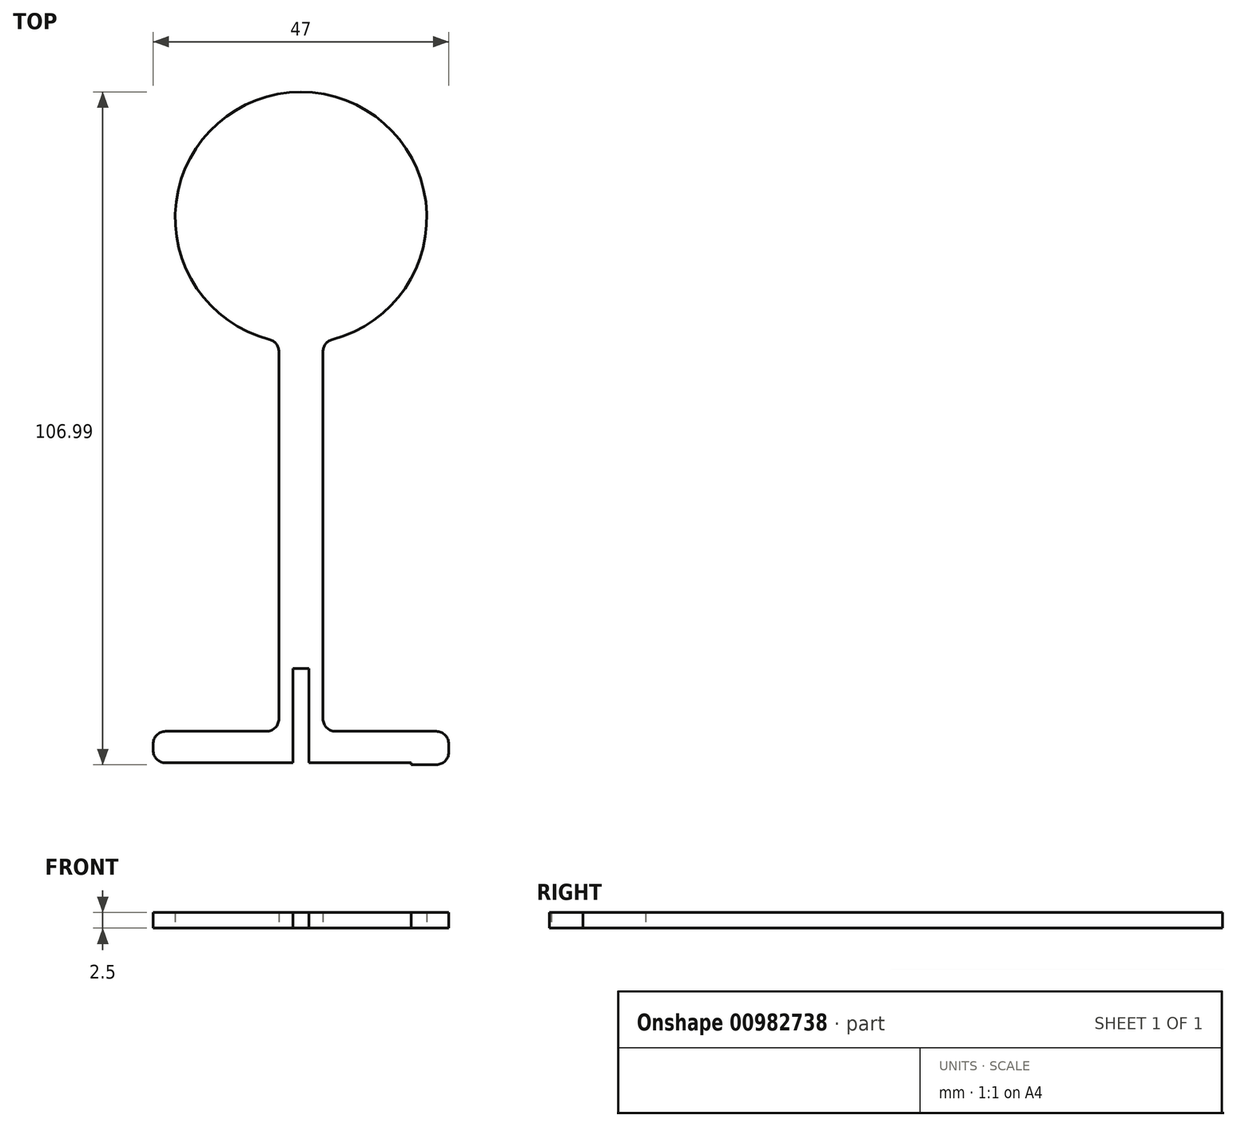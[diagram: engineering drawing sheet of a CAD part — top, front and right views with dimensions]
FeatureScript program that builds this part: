
annotation { "Feature Type Name" : "Feature", "Feature Type Description" : "" }
export const myFeature = defineFeature(function(context is Context, id is Id, definition is map)
    precondition{}
    {
        {
            var Q0;
            Q0=qCreatedBy(makeId("Top.planeOp"),FACE);
            var sketch = newSketch(context, id + "F0", { "sketchPlane" : qUnion([Q0])});
            skLineSegment(sketch, "E0", {"start": v(-3.5, -3) * mm, "end": v(-3.5, -65) * mm});
            skLineSegment(sketch, "E1", {"start": v(-3.5, -65) * mm, "end": v(-23.5, -65) * mm});
            skLineSegment(sketch, "E2", {"start": v(-23.5, -65) * mm, "end": v(-23.5, -70) * mm});
            skLineSegment(sketch, "E3", {"start": v(-23.5, -70) * mm, "end": v(23.5, -70) * mm});
            skLineSegment(sketch, "E4", {"start": v(23.5, -70) * mm, "end": v(23.5, -65) * mm});
            skLineSegment(sketch, "E5", {"start": v(23.5, -65) * mm, "end": v(3.5, -65) * mm});
            skLineSegment(sketch, "E6", {"start": v(3.5, -65) * mm, "end": v(3.5, -3) * mm});
            skLineSegment(sketch, "E7.bottom", {"start": v(1.25, -70) * mm, "end": v(-1.25, -70) * mm});
            skLineSegment(sketch, "E7.top", {"start": v(1.25, -55) * mm, "end": v(-1.25, -55) * mm});
            skLineSegment(sketch, "E7.left", {"start": v(1.25, -70) * mm, "end": v(1.25, -55) * mm});
            skLineSegment(sketch, "E7.right", {"start": v(-1.25, -70) * mm, "end": v(-1.25, -55) * mm});
            skPoint(sketch, "E7.middle", {"position": v(0, -62.5) * mm});
            skCircle(sketch, "E8", {"center": v(0, 16.7) * mm, "radius": 20 * mm});
            skLineSegment(sketch, "E9.bottom", {"start": v(-23.5, -70) * mm, "end": v(-17.5, -70) * mm});
            skLineSegment(sketch, "E9.top", {"start": v(-23.5, -70.3) * mm, "end": v(-17.5, -70.3) * mm});
            skLineSegment(sketch, "E9.left", {"start": v(-23.5, -70) * mm, "end": v(-23.5, -70.3) * mm});
            skLineSegment(sketch, "E9.right", {"start": v(-17.5, -70) * mm, "end": v(-17.5, -70.3) * mm});
            skLineSegment(sketch, "E10.MirrorCS", {"start": v(23.5, -70.3) * mm, "end": v(17.5, -70.3) * mm});
            skLineSegment(sketch, "E11.MirrorCS", {"start": v(23.5, -70) * mm, "end": v(17.5, -70) * mm});
            skLineSegment(sketch, "E12.MirrorCS", {"start": v(23.5, -70) * mm, "end": v(23.5, -70.3) * mm});
            skLineSegment(sketch, "E13.MirrorCS", {"start": v(17.5, -70) * mm, "end": v(17.5, -70.3) * mm});
            skSolve(sketch);
        }
        {
            var Q0;
            Q0=makeQuery(id+"F0.imprint","IMPRINT",FACE,{"disambiguationData":[TD([[makeQuery(id+"F0.imprint","IMPRINT",EDGE,{"derivedFrom":sQuery(id+"F0.wireOp",EDGE,"0U4RxweM-u2bA-2Qqt-OOBg-x1ftkZs6jUrD")}),1.0]])]});
            var Q1;
            {var subQ0=sQuery(id+"F0.wireOp",EDGE,"im0v1Rov-prSM-cwdN-f0IW-ScqFdnQkXUSi");Q1=makeQuery(id+"F0.imprint","IMPRINT",FACE,{"disambiguationData":[TD([[makeQuery(id+"F0.imprint","IMPRINT",EDGE,{"derivedFrom":subQ0}),1.0]])]});}
            var Q2;
            {var subQ7=sQuery(id+"F0.wireOp",EDGE,"E0");Q2=makeQuery(id+"F0.imprint","IMPRINT",FACE,{"disambiguationData":[TD([[makeQuery(id+"F0.imprint","IMPRINT",EDGE,{"derivedFrom":subQ7}),1.0]])]});}
            var Q3;
            {var subQ0=sQuery(id+"F0.wireOp",EDGE,"E8");var subQ1=makeQuery(id+"F0.imprint","INTERSECT",VERTEX,{"derivedFrom":[sQuery(id+"F0.wireOp",EDGE,"E0"),subQ0]});Q3=makeQuery(id+"F0.imprint","IMPRINT",FACE,{"disambiguationData":[TD([[makeQuery(id+"F0.imprint","IMPRINT",EDGE,{"disambiguationData":[TD([[subQ1,-1.0]])],"derivedFrom":subQ0}),1.0]])]});}
            var Q4;
            Q4=makeQuery(id+"F0.imprint","IMPRINT",FACE,{"disambiguationData":[TD([[makeQuery(id+"F0.imprint","IMPRINT",EDGE,{"derivedFrom":sQuery(id+"F0.wireOp",EDGE,"E9.bottom")}),-1.0]])]});
            var Q5;
            Q5=makeQuery(id+"F0.imprint","IMPRINT",FACE,{"disambiguationData":[TD([[makeQuery(id+"F0.imprint","IMPRINT",EDGE,{"derivedFrom":sQuery(id+"F0.wireOp",EDGE,"E10.MirrorCS")}),-1.0]])]});
            extrude(context, id + "F1", {"entities" : qUnion([Q0, Q1, Q2, Q3, Q4, Q5]), "flatOperationType" : FlatOperationType.REMOVE, "depth" : 2.5 * mm, "offsetDistance" : 25 * mm, "domain" : OperationDomain.MODEL});
        }
        {
            var Q0;
            Q0=makeQuery(id+"F1.opExtrude","SWEPT_EDGE",EDGE,{"disambiguationData":[OSD([sQuery(id+"F0.wireOp",EDGE,"E0"),sQuery(id+"F0.wireOp",EDGE,"E8")])]});
            var Q1;
            Q1=makeQuery(id+"F1.opExtrude","SWEPT_EDGE",EDGE,{"disambiguationData":[OSD([sQuery(id+"F0.wireOp",EDGE,"E6"),sQuery(id+"F0.wireOp",EDGE,"E8")])]});
            var Q2;
            Q2=makeQuery(id+"F1.opExtrude","SWEPT_EDGE",EDGE,{"disambiguationData":[OSD([sQuery(id+"F0.wireOp",EDGE,"E4"),sQuery(id+"F0.wireOp",EDGE,"E5")])]});
            var Q3;
            Q3=makeQuery(id+"F1.opExtrude","SWEPT_EDGE",EDGE,{"disambiguationData":[OSD([sQuery(id+"F0.wireOp",EDGE,"E1"),sQuery(id+"F0.wireOp",EDGE,"E2")])]});
            var Q4;
            Q4=makeQuery(id+"F1.opExtrude","SWEPT_EDGE",EDGE,{"disambiguationData":[OSD([sQuery(id+"F0.wireOp",EDGE,"E0"),sQuery(id+"F0.wireOp",EDGE,"E1")])]});
            var Q5;
            Q5=makeQuery(id+"F1.opExtrude","SWEPT_EDGE",EDGE,{"disambiguationData":[OSD([sQuery(id+"F0.wireOp",EDGE,"E5"),sQuery(id+"F0.wireOp",EDGE,"E6")])]});
            var Q6;
            Q6=makeQuery(id+"F1.opExtrude","SWEPT_EDGE",EDGE,{"disambiguationData":[OSD([sQuery(id+"F0.wireOp",EDGE,"E9.top"),sQuery(id+"F0.wireOp",EDGE,"E9.left")])]});
            var Q7;
            Q7=makeQuery(id+"F1.opExtrude","SWEPT_EDGE",EDGE,{"disambiguationData":[OSD([sQuery(id+"F0.wireOp",EDGE,"E10.MirrorCS"),sQuery(id+"F0.wireOp",EDGE,"E12.MirrorCS")])]});
            fillet(context, id + "F2", {"entities" : qUnion([Q0, Q1, Q2, Q3, Q4, Q5, Q6, Q7]), "radius" : 2 * mm, "tangentPropagation" : true, "allowEdgeOverflow" : false});
        }
    });
